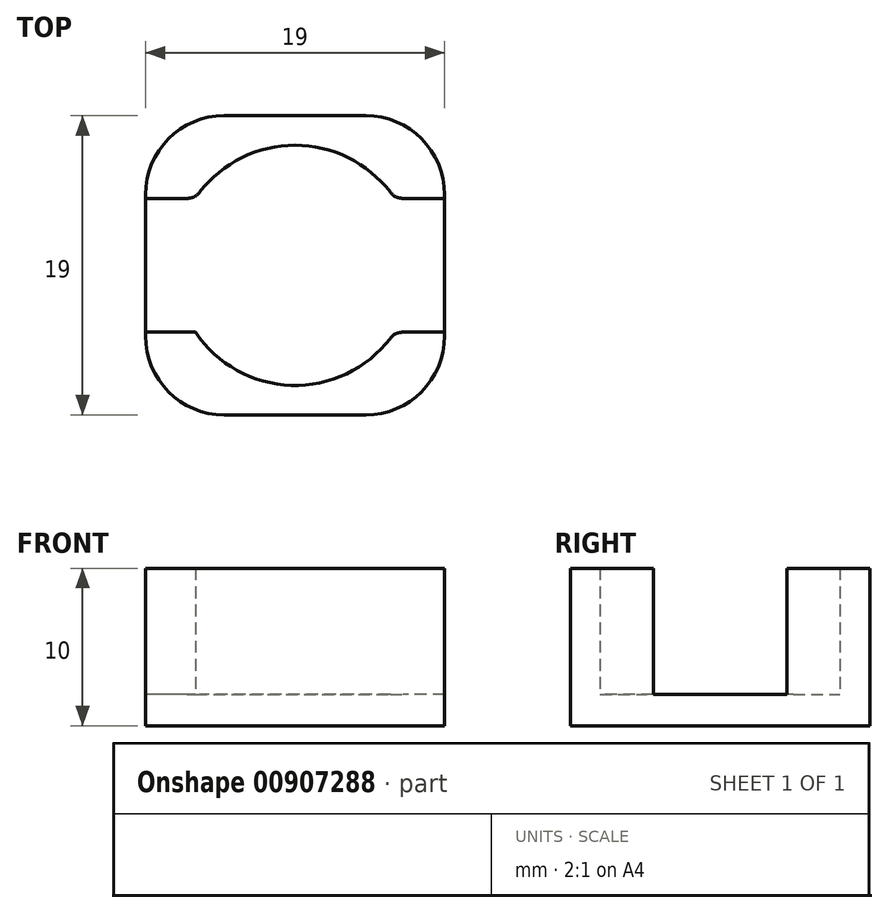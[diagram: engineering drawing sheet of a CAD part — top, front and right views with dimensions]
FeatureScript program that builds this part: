
annotation { "Feature Type Name" : "Feature", "Feature Type Description" : "" }
export const myFeature = defineFeature(function(context is Context, id is Id, definition is map)
    precondition{}
    {
        {
            var Q0;
            Q0=qCreatedBy(makeId("Top.planeOp"),FACE);
            var sketch = newSketch(context, id + "F0", { "sketchPlane" : qUnion([Q0])});
            skLineSegment(sketch, "E0.bottom", {"start": v(9.5, -9.5) * mm, "end": v(-9.5, -9.5) * mm});
            skLineSegment(sketch, "E0.top", {"start": v(9.5, 9.5) * mm, "end": v(-9.5, 9.5) * mm});
            skLineSegment(sketch, "E0.left", {"start": v(9.5, -9.5) * mm, "end": v(9.5, 9.5) * mm});
            skLineSegment(sketch, "E0.right", {"start": v(-9.5, -9.5) * mm, "end": v(-9.5, 9.5) * mm});
            skPoint(sketch, "E0.middle", {"position": v(0, 0) * mm});
            skSolve(sketch);
        }
        {
            var Q0;
            Q0=makeQuery(id+"F0.imprint","IMPRINT",FACE,{"disambiguationData":[TD([[makeQuery(id+"F0.imprint","IMPRINT",EDGE,{"derivedFrom":sQuery(id+"F0.wireOp",EDGE,"E0.bottom")}),-1.0]])]});
            extrude(context, id + "F1", {"entities" : qUnion([Q0]), "depth" : 2 * mm, "offsetDistance" : 25 * mm});
        }
        {
            var Q0;
            Q0=makeQuery(id+"F1.opExtrude","CAP_FACE",FACE,{"disambiguationData":[OSD([sQuery(id+"F0.wireOp",EDGE,"E0.bottom"),sQuery(id+"F0.wireOp",EDGE,"E0.top"),sQuery(id+"F0.wireOp",EDGE,"E0.left"),sQuery(id+"F0.wireOp",EDGE,"E0.right")])],"isStart":false});
            var sketch = newSketch(context, id + "F2", { "sketchPlane" : qUnion([Q0])});
            skPoint(sketch, "E1.middle", {"position": v(0, 0) * mm});
            skCircle(sketch, "E2", {"center": v(0, 0) * mm, "radius": 7.62 * mm});
            skPoint(sketch, "E3", {"position": v(-6.33, 4.25) * mm});
            skPoint(sketch, "E4", {"position": v(6.33, -4.25) * mm});
            skPoint(sketch, "E5", {"position": v(-6.33, -4.25) * mm});
            skPoint(sketch, "E6", {"position": v(6.33, 4.25) * mm});
            skLineSegment(sketch, "E7.bottom", {"start": v(9.5, -4.25) * mm, "end": v(-9.5, -4.25) * mm});
            skLineSegment(sketch, "E7.top", {"start": v(9.5, 4.25) * mm, "end": v(-9.5, 4.25) * mm});
            skLineSegment(sketch, "E7.left", {"start": v(9.5, -4.25) * mm, "end": v(9.5, 4.25) * mm});
            skLineSegment(sketch, "E7.right", {"start": v(-9.5, -4.25) * mm, "end": v(-9.5, 4.25) * mm});
            skSolve(sketch);
        }
        {
            var Q0;
            {var subQ0=makeQuery(id+"F1.opExtrude","CAP_EDGE",EDGE,{"disambiguationData":[OSD([sQuery(id+"F0.wireOp",EDGE,"E0.bottom")])],"isStart":false});Q0=makeQuery(id+"F2.imprint","IMPRINT",FACE,{"disambiguationData":[TD([[makeQuery(id+"F2.imprint","IMPRINT",EDGE,{"derivedFrom":subQ0}),-1.0]])]});}
            var Q1;
            {var subQ0=makeQuery(id+"F1.opExtrude","CAP_EDGE",EDGE,{"disambiguationData":[OSD([sQuery(id+"F0.wireOp",EDGE,"E0.top")])],"isStart":false});Q1=makeQuery(id+"F2.imprint","IMPRINT",FACE,{"disambiguationData":[TD([[makeQuery(id+"F2.imprint","IMPRINT",EDGE,{"derivedFrom":subQ0}),1.0]])]});}
            extrude(context, id + "F3", {"entities" : qUnion([Q0, Q1]), "operationType" : NewBodyOperationType.ADD, "depth" : 8 * mm, "offsetDistance" : 25 * mm});
        }
        {
            var Q0;
            Q0=makeQuery(id+"F3.boolean.opBoolean","MERGE",EDGE,{"derivedFrom":[makeQuery(id+"F1.opExtrude","SWEPT_EDGE",EDGE,{"disambiguationData":[OSD([sQuery(id+"F0.wireOp",EDGE,"E0.bottom"),sQuery(id+"F0.wireOp",EDGE,"E0.right")])]}),makeQuery(id+"F3.opExtrude","SWEPT_EDGE",EDGE,{"disambiguationData":[OSD([sQuery(id+"F2.wireOp",EDGE,"E1.bottom"),sQuery(id+"F2.wireOp",EDGE,"E1.right")])]})]});
            var Q1;
            Q1=makeQuery(id+"F3.boolean.opBoolean","MERGE",EDGE,{"derivedFrom":[makeQuery(id+"F1.opExtrude","SWEPT_EDGE",EDGE,{"disambiguationData":[OSD([sQuery(id+"F0.wireOp",EDGE,"E0.bottom"),sQuery(id+"F0.wireOp",EDGE,"E0.left")])]}),makeQuery(id+"F3.opExtrude","SWEPT_EDGE",EDGE,{"disambiguationData":[OSD([sQuery(id+"F2.wireOp",EDGE,"E1.bottom"),sQuery(id+"F2.wireOp",EDGE,"E1.left")])]})]});
            var Q2;
            Q2=makeQuery(id+"F3.boolean.opBoolean","MERGE",EDGE,{"derivedFrom":[makeQuery(id+"F1.opExtrude","SWEPT_EDGE",EDGE,{"disambiguationData":[OSD([sQuery(id+"F0.wireOp",EDGE,"E0.top"),sQuery(id+"F0.wireOp",EDGE,"E0.left")])]}),makeQuery(id+"F3.opExtrude","SWEPT_EDGE",EDGE,{"disambiguationData":[OSD([sQuery(id+"F2.wireOp",EDGE,"E1.top"),sQuery(id+"F2.wireOp",EDGE,"E1.left")])]})]});
            var Q3;
            Q3=makeQuery(id+"F3.boolean.opBoolean","MERGE",EDGE,{"derivedFrom":[makeQuery(id+"F1.opExtrude","SWEPT_EDGE",EDGE,{"disambiguationData":[OSD([sQuery(id+"F0.wireOp",EDGE,"E0.top"),sQuery(id+"F0.wireOp",EDGE,"E0.right")])]}),makeQuery(id+"F3.opExtrude","SWEPT_EDGE",EDGE,{"disambiguationData":[OSD([sQuery(id+"F2.wireOp",EDGE,"E1.top"),sQuery(id+"F2.wireOp",EDGE,"E1.right")])]})]});
            fillet(context, id + "F4", {"entities" : qUnion([Q0, Q1, Q2, Q3]), "radius" : 5 * mm, "tangentPropagation" : true, "allowEdgeOverflow" : false});
        }
        {
            var Q0;
            {var subQ0=sQuery(id+"F2.wireOp",EDGE,"E7.top");var subQ1=sQuery(id+"F0.wireOp",EDGE,"E0.right");var subQ2=sQuery(id+"F0.wireOp",EDGE,"E0.top");Q0=makeQuery(id+"F4.opFillet","BLEND_EDGE",EDGE,{"blendedFrom":[makeQuery(id+"F3.boolean.opBoolean","MERGE",EDGE,{"derivedFrom":[makeQuery(id+"F1.opExtrude","SWEPT_EDGE",EDGE,{"disambiguationData":[OSD([subQ2,subQ1])]}),makeQuery(id+"F3.opExtrude","SWEPT_EDGE",EDGE,{"disambiguationData":[OSD([subQ2,subQ1])]})]}),makeQuery(id+"F3.opExtrude","SWEPT_FACE",FACE,{"disambiguationData":[OSD([subQ0]),TDD([makeQuery(id+"F2.imprint","IMPRINT",EDGE,{"disambiguationData":[TD([[makeQuery(id+"F2.imprint","INTERSECT",VERTEX,{"disambiguationData":[OD(0.0)],"derivedFrom":[sQuery(id+"F2.wireOp",EDGE,"E2"),subQ0]}),-1.0]])],"derivedFrom":subQ0})])]})],"blendedInto":[makeQuery(id+"F3.opExtrude","SWEPT_FACE",FACE,{"disambiguationData":[OSD([subQ0]),TDD([makeQuery(id+"F2.imprint","IMPRINT",EDGE,{"disambiguationData":[TD([[makeQuery(id+"F2.imprint","INTERSECT",VERTEX,{"disambiguationData":[OD(0.0)],"derivedFrom":[sQuery(id+"F2.wireOp",EDGE,"E2"),subQ0]}),-1.0]])],"derivedFrom":subQ0})])]})]});}
            var Q1;
            {var subQ0=sQuery(id+"F2.wireOp",EDGE,"E7.top");var subQ1=sQuery(id+"F2.wireOp",EDGE,"E2");Q1=makeQuery(id+"F3.opExtrude","SWEPT_EDGE",EDGE,{"disambiguationData":[OSD([subQ1,subQ0]),TDD([makeQuery(id+"F2.imprint","INTERSECT",VERTEX,{"disambiguationData":[OD(0.0)],"derivedFrom":[subQ1,subQ0]})])]});}
            var Q2;
            {var subQ0=sQuery(id+"F2.wireOp",EDGE,"E7.top");var subQ1=sQuery(id+"F2.wireOp",EDGE,"E2");Q2=makeQuery(id+"F3.opExtrude","SWEPT_EDGE",EDGE,{"disambiguationData":[OSD([subQ1,subQ0]),TDD([makeQuery(id+"F2.imprint","INTERSECT",VERTEX,{"disambiguationData":[OD(1.0)],"derivedFrom":[subQ1,subQ0]})])]});}
            var Q3;
            {var subQ0=sQuery(id+"F2.wireOp",EDGE,"E7.top");var subQ1=sQuery(id+"F0.wireOp",EDGE,"E0.left");var subQ2=sQuery(id+"F0.wireOp",EDGE,"E0.top");Q3=makeQuery(id+"F4.opFillet","BLEND_EDGE",EDGE,{"blendedFrom":[makeQuery(id+"F3.boolean.opBoolean","MERGE",EDGE,{"derivedFrom":[makeQuery(id+"F1.opExtrude","SWEPT_EDGE",EDGE,{"disambiguationData":[OSD([subQ2,subQ1])]}),makeQuery(id+"F3.opExtrude","SWEPT_EDGE",EDGE,{"disambiguationData":[OSD([subQ2,subQ1])]})]}),makeQuery(id+"F3.opExtrude","SWEPT_FACE",FACE,{"disambiguationData":[OSD([subQ0]),TDD([makeQuery(id+"F2.imprint","IMPRINT",EDGE,{"disambiguationData":[TD([[makeQuery(id+"F2.imprint","INTERSECT",VERTEX,{"disambiguationData":[OD(1.0)],"derivedFrom":[sQuery(id+"F2.wireOp",EDGE,"E2"),subQ0]}),1.0]])],"derivedFrom":subQ0})])]})],"blendedInto":[makeQuery(id+"F3.opExtrude","SWEPT_FACE",FACE,{"disambiguationData":[OSD([subQ0]),TDD([makeQuery(id+"F2.imprint","IMPRINT",EDGE,{"disambiguationData":[TD([[makeQuery(id+"F2.imprint","INTERSECT",VERTEX,{"disambiguationData":[OD(1.0)],"derivedFrom":[sQuery(id+"F2.wireOp",EDGE,"E2"),subQ0]}),1.0]])],"derivedFrom":subQ0})])]})]});}
            var Q4;
            {var subQ0=sQuery(id+"F2.wireOp",EDGE,"E7.bottom");var subQ1=sQuery(id+"F0.wireOp",EDGE,"E0.left");var subQ2=sQuery(id+"F0.wireOp",EDGE,"E0.bottom");Q4=makeQuery(id+"F4.opFillet","BLEND_EDGE",EDGE,{"blendedFrom":[makeQuery(id+"F3.boolean.opBoolean","MERGE",EDGE,{"derivedFrom":[makeQuery(id+"F1.opExtrude","SWEPT_EDGE",EDGE,{"disambiguationData":[OSD([subQ2,subQ1])]}),makeQuery(id+"F3.opExtrude","SWEPT_EDGE",EDGE,{"disambiguationData":[OSD([subQ2,subQ1])]})]}),makeQuery(id+"F3.opExtrude","SWEPT_FACE",FACE,{"disambiguationData":[OSD([subQ0]),TDD([makeQuery(id+"F2.imprint","IMPRINT",EDGE,{"disambiguationData":[TD([[makeQuery(id+"F2.imprint","INTERSECT",VERTEX,{"disambiguationData":[OD(1.0)],"derivedFrom":[sQuery(id+"F2.wireOp",EDGE,"E2"),subQ0]}),1.0]])],"derivedFrom":subQ0})])]})],"blendedInto":[makeQuery(id+"F3.opExtrude","SWEPT_FACE",FACE,{"disambiguationData":[OSD([subQ0]),TDD([makeQuery(id+"F2.imprint","IMPRINT",EDGE,{"disambiguationData":[TD([[makeQuery(id+"F2.imprint","INTERSECT",VERTEX,{"disambiguationData":[OD(1.0)],"derivedFrom":[sQuery(id+"F2.wireOp",EDGE,"E2"),subQ0]}),1.0]])],"derivedFrom":subQ0})])]})]});}
            var Q5;
            {var subQ0=sQuery(id+"F2.wireOp",EDGE,"E7.bottom");var subQ1=sQuery(id+"F2.wireOp",EDGE,"E2");Q5=makeQuery(id+"F3.opExtrude","SWEPT_EDGE",EDGE,{"disambiguationData":[OSD([subQ1,subQ0]),TDD([makeQuery(id+"F2.imprint","INTERSECT",VERTEX,{"disambiguationData":[OD(0.0)],"derivedFrom":[subQ1,subQ0]})])]});}
            var Q6;
            {var subQ0=sQuery(id+"F2.wireOp",EDGE,"E7.bottom");var subQ1=sQuery(id+"F0.wireOp",EDGE,"E0.right");var subQ2=sQuery(id+"F0.wireOp",EDGE,"E0.bottom");Q6=makeQuery(id+"F4.opFillet","BLEND_EDGE",EDGE,{"blendedFrom":[makeQuery(id+"F3.boolean.opBoolean","MERGE",EDGE,{"derivedFrom":[makeQuery(id+"F1.opExtrude","SWEPT_EDGE",EDGE,{"disambiguationData":[OSD([subQ2,subQ1])]}),makeQuery(id+"F3.opExtrude","SWEPT_EDGE",EDGE,{"disambiguationData":[OSD([subQ2,subQ1])]})]}),makeQuery(id+"F3.opExtrude","SWEPT_FACE",FACE,{"disambiguationData":[OSD([subQ0]),TDD([makeQuery(id+"F2.imprint","IMPRINT",EDGE,{"disambiguationData":[TD([[makeQuery(id+"F2.imprint","INTERSECT",VERTEX,{"disambiguationData":[OD(0.0)],"derivedFrom":[sQuery(id+"F2.wireOp",EDGE,"E2"),subQ0]}),-1.0]])],"derivedFrom":subQ0})])]})],"blendedInto":[makeQuery(id+"F3.opExtrude","SWEPT_FACE",FACE,{"disambiguationData":[OSD([subQ0]),TDD([makeQuery(id+"F2.imprint","IMPRINT",EDGE,{"disambiguationData":[TD([[makeQuery(id+"F2.imprint","INTERSECT",VERTEX,{"disambiguationData":[OD(0.0)],"derivedFrom":[sQuery(id+"F2.wireOp",EDGE,"E2"),subQ0]}),-1.0]])],"derivedFrom":subQ0})])]})]});}
            fillet(context, id + "F5", {"entities" : qUnion([Q0, Q1, Q2, Q3, Q4, Q5, Q6]), "radius" : 1 * mm, "tangentPropagation" : true, "allowEdgeOverflow" : false});
        }
    });
